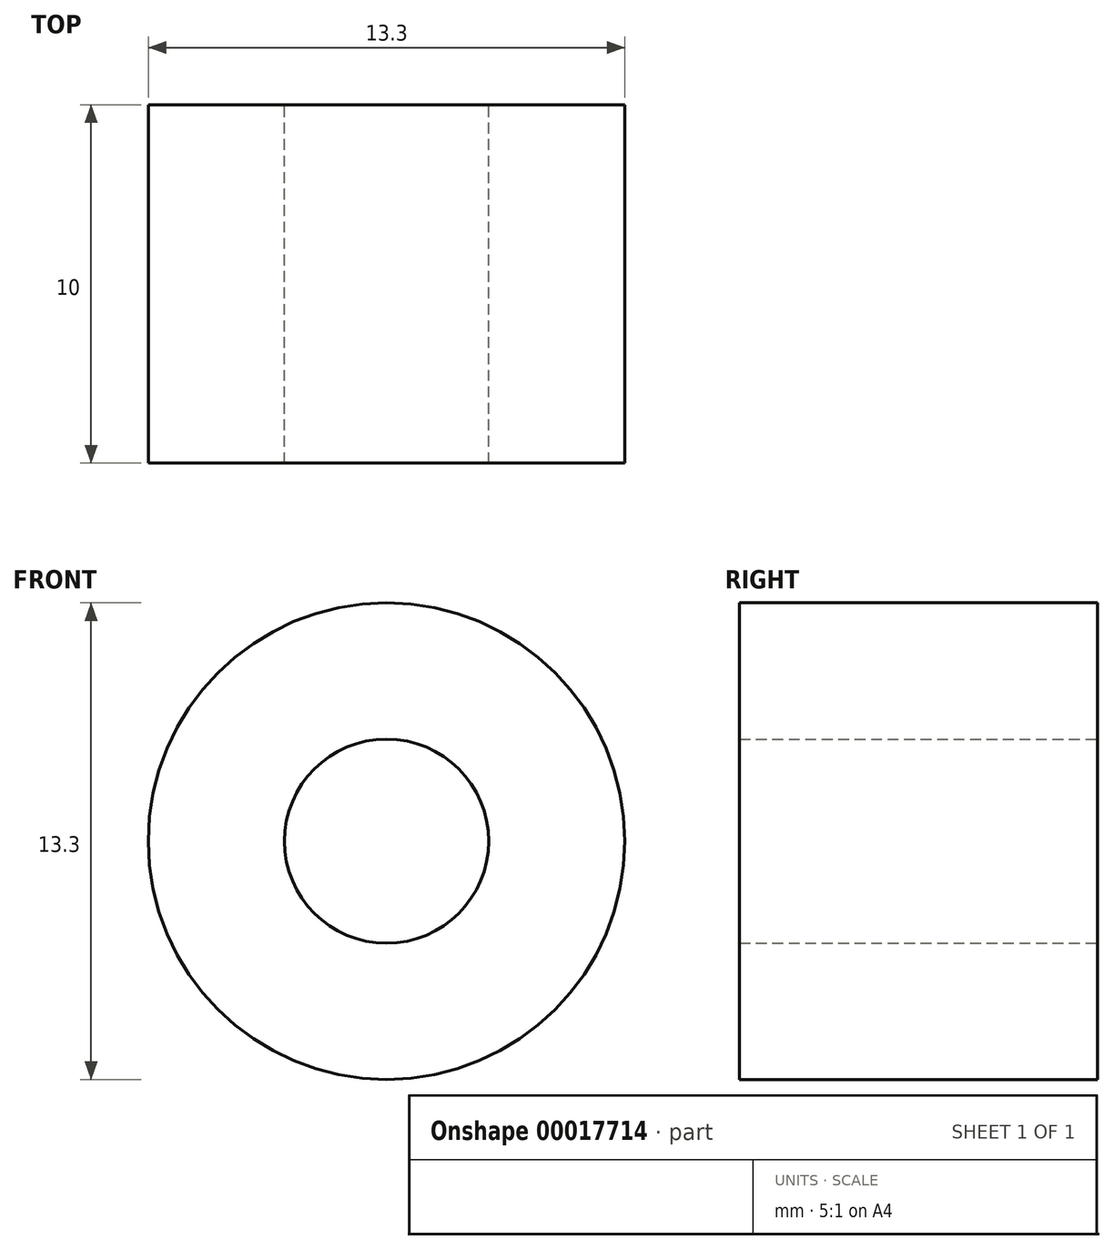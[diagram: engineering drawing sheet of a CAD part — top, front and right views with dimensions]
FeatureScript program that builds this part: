
annotation { "Feature Type Name" : "Feature", "Feature Type Description" : "" }
export const myFeature = defineFeature(function(context is Context, id is Id, definition is map)
    precondition{}
    {
        {
            var Q0;
            Q0=qCreatedBy(makeId("Front.planeOp"),FACE);
            var sketch = newSketch(context, id + "F0", { "sketchPlane" : qUnion([Q0])});
            skCircle(sketch, "E0", {"center": v(0, 0) * mm, "radius": 6.65 * mm});
            skCircle(sketch, "E1", {"center": v(0, 0) * mm, "radius": 2.85 * mm});
            skSolve(sketch);
        }
        {
            var Q0;
            Q0=makeQuery(id+"F0.imprint","IMPRINT",FACE,{"disambiguationData":[TD([[makeQuery(id+"F0.imprint","IMPRINT",EDGE,{"derivedFrom":sQuery(id+"F0.wireOp",EDGE,"E0")}),1.0]])]});
            extrude(context, id + "F1", {"entities" : qUnion([Q0]), "depth" : 10 * mm});
        }
    });
